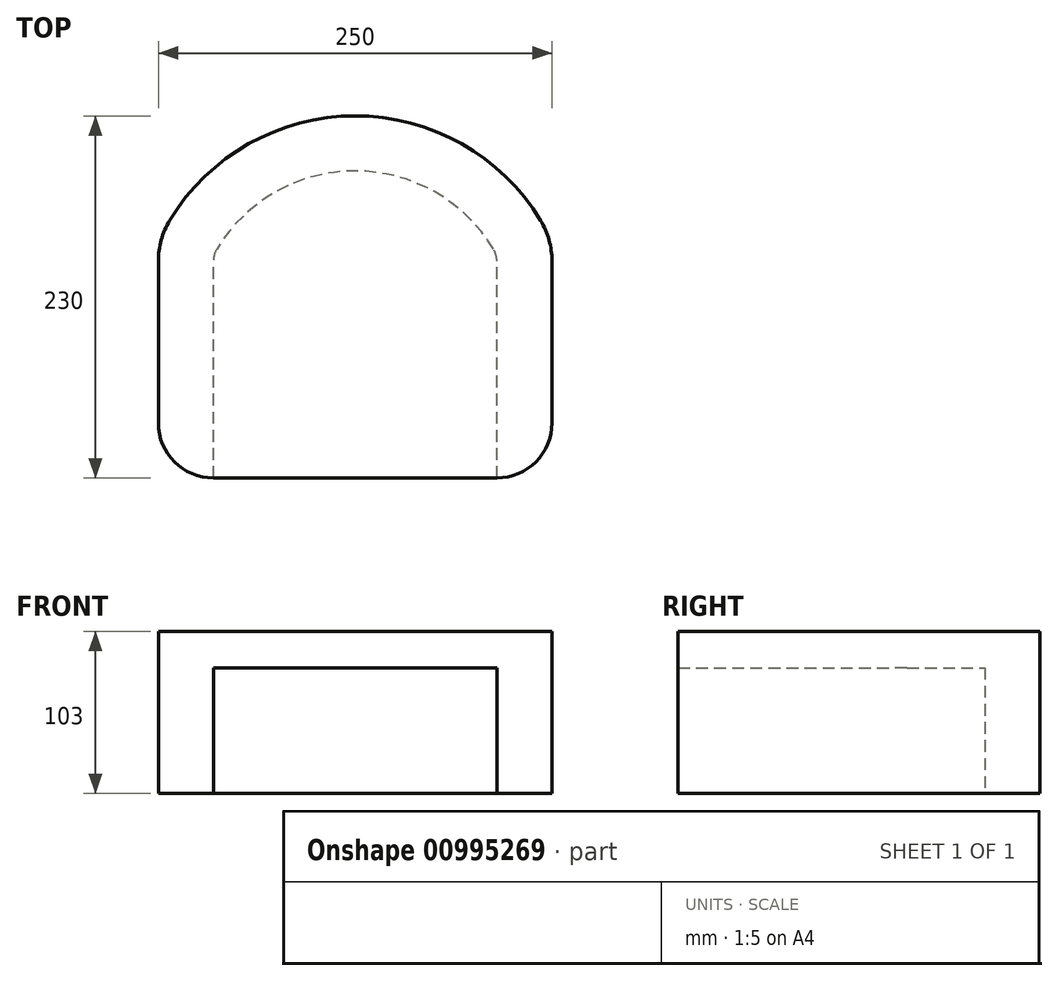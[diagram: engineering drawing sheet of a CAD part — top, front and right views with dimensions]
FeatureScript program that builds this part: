
annotation { "Feature Type Name" : "Feature", "Feature Type Description" : "" }
export const myFeature = defineFeature(function(context is Context, id is Id, definition is map)
    precondition{}
    {
        {
            var Q0;
            Q0=qCreatedBy(makeId("Top.planeOp"),FACE);
            var sketch = newSketch(context, id + "F0", { "sketchPlane" : qUnion([Q0])});
            skLineSegment(sketch, "E0.bottom", {"start": v(90, -115) * mm, "end": v(-90, -115) * mm});
            skLineSegment(sketch, "E0.left", {"start": v(125, -80) * mm, "end": v(125, 22.72) * mm});
            skLineSegment(sketch, "E0.right", {"start": v(-125, -80) * mm, "end": v(-125, 22.72) * mm});
            skPoint(sketch, "E0.middle", {"position": v(0, 0) * mm});
            skLineSegment(sketch, "E1", {"start": v(0, 115) * mm, "end": v(0, -115) * mm, "construction": true});
            skArc(sketch, "E2", {"start": v(117.78, 48.6) * mm, "mid": v(0, 115) * mm, "end": v(-117.78, 48.6) * mm});
            skPoint(sketch, "E3.orphan", {"position": v(-125, 115) * mm});
            skPoint(sketch, "E4.orphan", {"position": v(125, 115) * mm});
            skPoint(sketch, "E5.visualSharp", {"position": v(-125, 35) * mm});
            skArc(sketch, "E5.filletArc", {"start": v(-117.78, 48.6) * mm, "mid": v(-123.16, 36.15) * mm, "end": v(-125, 22.72) * mm});
            skPoint(sketch, "E6.visualSharp", {"position": v(125, 35) * mm});
            skArc(sketch, "E6.filletArc", {"start": v(125, 22.72) * mm, "mid": v(123.16, 36.15) * mm, "end": v(117.78, 48.6) * mm});
            skPoint(sketch, "E7.visualSharp", {"position": v(-125, -115) * mm});
            skArc(sketch, "E7.filletArc", {"start": v(-125, -80) * mm, "mid": v(-114.75, -104.75) * mm, "end": v(-90, -115) * mm});
            skPoint(sketch, "E8.visualSharp", {"position": v(125, -115) * mm});
            skArc(sketch, "E8.filletArc", {"start": v(90, -115) * mm, "mid": v(114.75, -104.75) * mm, "end": v(125, -80) * mm});
            skSolve(sketch);
        }
        {
            var Q0;
            Q0 = qSketchRegion(id + "F0", true);
            extrude(context, id + "F1", {"entities" : qUnion([Q0]), "depth" : 103 * mm, "offsetDistance" : 25 * mm});
        }
        {
            var Q0;
            Q0=qCreatedBy(makeId("Top.planeOp"),FACE);
            var sketch = newSketch(context, id + "F2", { "sketchPlane" : qUnion([Q0])});
            skLineSegment(sketch, "E9.0", {"start": v(90, -133.3) * mm, "end": v(90, 22.72) * mm});
            skLineSegment(sketch, "E9.1", {"start": v(-90, -133.3) * mm, "end": v(-90, 22.72) * mm});
            skArc(sketch, "E9.2", {"start": v(-87.83, 30.48) * mm, "mid": v(-89.45, 26.75) * mm, "end": v(-90, 22.72) * mm});
            skArc(sketch, "E9.3", {"start": v(87.83, 30.48) * mm, "mid": v(0, 80) * mm, "end": v(-87.83, 30.48) * mm});
            skArc(sketch, "E9.4", {"start": v(90, 22.72) * mm, "mid": v(89.45, 26.75) * mm, "end": v(87.83, 30.48) * mm});
            skLineSegment(sketch, "E10", {"start": v(-90, -133.3) * mm, "end": v(90, -133.3) * mm});
            skSolve(sketch);
        }
        {
            var Q0;
            Q0=makeQuery(id+"F2.imprint","IMPRINT",FACE,{"disambiguationData":[TD([[makeQuery(id+"F2.imprint","IMPRINT",EDGE,{"derivedFrom":sQuery(id+"F2.wireOp",EDGE,"E9.0")}),1.0]])]});
            extrude(context, id + "F3", {"entities" : qUnion([Q0]), "operationType" : NewBodyOperationType.REMOVE, "depth" : 80 * mm, "offsetDistance" : 25 * mm});
        }
    });
